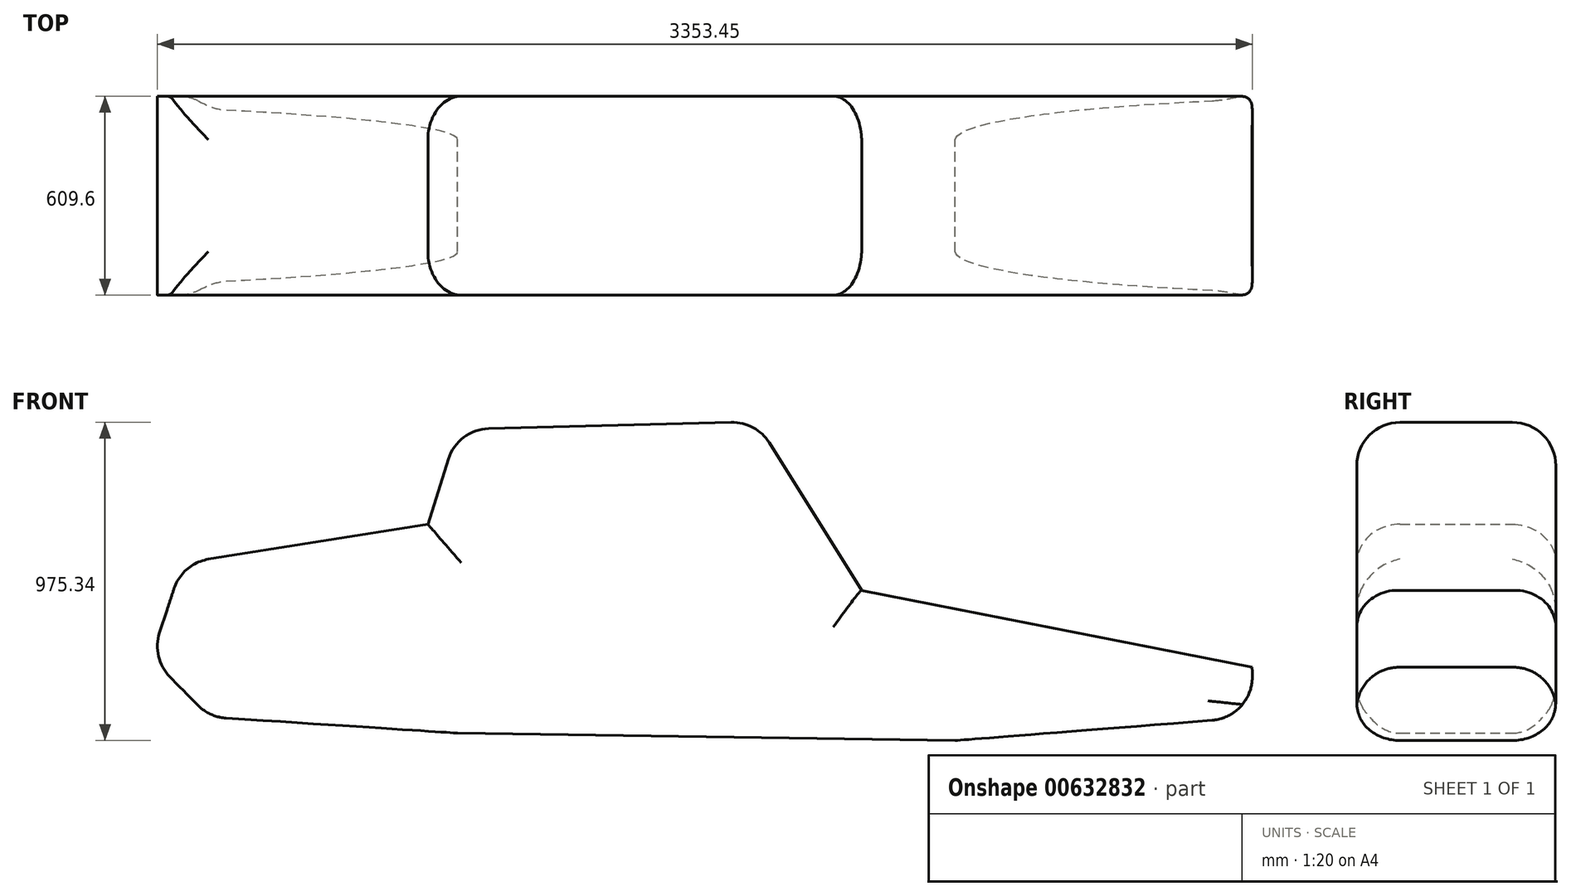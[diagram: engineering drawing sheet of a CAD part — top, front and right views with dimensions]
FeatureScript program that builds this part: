
annotation { "Feature Type Name" : "Feature", "Feature Type Description" : "" }
export const myFeature = defineFeature(function(context is Context, id is Id, definition is map)
    precondition{}
    {
        {
            var Q0;
            Q0=qCreatedBy(makeId("Front.planeOp"),FACE);
            var sketch = newSketch(context, id + "F0", { "sketchPlane" : qUnion([Q0])});
            skLineSegment(sketch, "E0", {"start": v(-2526.52, 590.94) * mm, "end": v(-3279.03, 471.06) * mm});
            skLineSegment(sketch, "E1", {"start": v(-3279.03, 471.06) * mm, "end": v(-3373.67, 181.32) * mm});
            skLineSegment(sketch, "E2", {"start": v(-2526.52, 590.94) * mm, "end": v(-2435.4, 881.8) * mm});
            skLineSegment(sketch, "E3", {"start": v(0, 0) * mm, "end": v(-2.12, 152.39) * mm});
            skLineSegment(sketch, "E4", {"start": v(-2.12, 152.39) * mm, "end": v(-1198.27, 388.33) * mm});
            skLineSegment(sketch, "E5", {"start": v(-1198.27, 388.33) * mm, "end": v(-1521.3, 905.3) * mm});
            skLineSegment(sketch, "E6", {"start": v(-1521.3, 905.3) * mm, "end": v(-2435.4, 881.8) * mm});
            skPoint(sketch, "E7.end.orphan", {"position": v(-2435.4, -49.28) * mm});
            skLineSegment(sketch, "E8", {"start": v(0, 0) * mm, "end": v(-911.57, -71.94) * mm});
            skPoint(sketch, "E9.start.orphan", {"position": v(-3279.03, 0) * mm});
            skLineSegment(sketch, "E10", {"start": v(-3373.67, 181.32) * mm, "end": v(-3195.8, 0) * mm});
            skLineSegment(sketch, "E11", {"start": v(-3195.8, 0) * mm, "end": v(-2435.4, -49.28) * mm});
            skLineSegment(sketch, "E12", {"start": v(-911.57, -71.94) * mm, "end": v(-2435.4, -49.28) * mm});
            skSolve(sketch);
        }
        {
            var Q0;
            Q0=makeQuery(id+"F0.imprint","IMPRINT",FACE,{"disambiguationData":[TD([[makeQuery(id+"F0.imprint","IMPRINT",EDGE,{"derivedFrom":sQuery(id+"F0.wireOp",EDGE,"E0")}),1.0]])]});
            extrude(context, id + "F1", {"entities" : qUnion([Q0]), "depth" : 609.6 * mm, "offsetDistance" : 25.4 * mm});
        }
        {
            var Q0;
            Q0=makeQuery(id+"F1.opExtrude","CAP_EDGE",EDGE,{"disambiguationData":[OSD([sQuery(id+"F0.wireOp",EDGE,"E4")])],"isStart":true});
            var Q1;
            Q1=makeQuery(id+"F1.opExtrude","CAP_EDGE",EDGE,{"disambiguationData":[OSD([sQuery(id+"F0.wireOp",EDGE,"E4")])],"isStart":false});
            fillet(context, id + "F2", {"entities" : qUnion([Q0, Q1]), "radius" : 127 * mm, "tangentPropagation" : true, "allowEdgeOverflow" : false});
        }
        {
            var Q0;
            Q0=makeQuery(id+"F1.opExtrude","CAP_EDGE",EDGE,{"disambiguationData":[OSD([sQuery(id+"F0.wireOp",EDGE,"E5")])],"isStart":false});
            var Q1;
            Q1=makeQuery(id+"F1.opExtrude","CAP_EDGE",EDGE,{"disambiguationData":[OSD([sQuery(id+"F0.wireOp",EDGE,"E5")])],"isStart":true});
            var Q2;
            Q2=makeQuery(id+"F1.opExtrude","CAP_EDGE",EDGE,{"disambiguationData":[OSD([sQuery(id+"F0.wireOp",EDGE,"E6")])],"isStart":false});
            var Q3;
            Q3=makeQuery(id+"F1.opExtrude","CAP_EDGE",EDGE,{"disambiguationData":[OSD([sQuery(id+"F0.wireOp",EDGE,"E6")])],"isStart":true});
            var Q4;
            Q4=makeQuery(id+"F1.opExtrude","SWEPT_EDGE",EDGE,{"disambiguationData":[OSD([sQuery(id+"F0.wireOp",EDGE,"E5"),sQuery(id+"F0.wireOp",EDGE,"E6")])]});
            var Q5;
            Q5=makeQuery(id+"F1.opExtrude","SWEPT_EDGE",EDGE,{"disambiguationData":[OSD([sQuery(id+"F0.wireOp",EDGE,"E2"),sQuery(id+"F0.wireOp",EDGE,"E6")])]});
            var Q6;
            Q6=makeQuery(id+"F1.opExtrude","CAP_EDGE",EDGE,{"disambiguationData":[OSD([sQuery(id+"F0.wireOp",EDGE,"E0")])],"isStart":false});
            var Q7;
            Q7=makeQuery(id+"F1.opExtrude","CAP_EDGE",EDGE,{"disambiguationData":[OSD([sQuery(id+"F0.wireOp",EDGE,"E0")])],"isStart":true});
            var Q8;
            Q8=makeQuery(id+"F1.opExtrude","SWEPT_EDGE",EDGE,{"disambiguationData":[OSD([sQuery(id+"F0.wireOp",EDGE,"E0"),sQuery(id+"F0.wireOp",EDGE,"E1")])]});
            var Q9;
            Q9=makeQuery(id+"F1.opExtrude","SWEPT_EDGE",EDGE,{"disambiguationData":[OSD([sQuery(id+"F0.wireOp",EDGE,"E1"),sQuery(id+"F0.wireOp",EDGE,"E10")])]});
            var Q10;
            Q10=makeQuery(id+"F1.opExtrude","SWEPT_EDGE",EDGE,{"disambiguationData":[OSD([sQuery(id+"F0.wireOp",EDGE,"E10"),sQuery(id+"F0.wireOp",EDGE,"E11")])]});
            var Q11;
            Q11=makeQuery(id+"F1.opExtrude","CAP_EDGE",EDGE,{"disambiguationData":[OSD([sQuery(id+"F0.wireOp",EDGE,"E12")])],"isStart":false});
            var Q12;
            Q12=makeQuery(id+"F1.opExtrude","CAP_EDGE",EDGE,{"disambiguationData":[OSD([sQuery(id+"F0.wireOp",EDGE,"E12")])],"isStart":true});
            var Q13;
            Q13=makeQuery(id+"F1.opExtrude","SWEPT_EDGE",EDGE,{"disambiguationData":[OSD([sQuery(id+"F0.wireOp",EDGE,"E3"),sQuery(id+"F0.wireOp",EDGE,"E8")])]});
            var Q14;
            Q14=makeQuery(id+"F1.opExtrude","CAP_EDGE",EDGE,{"disambiguationData":[OSD([sQuery(id+"F0.wireOp",EDGE,"E2")])],"isStart":false});
            var Q15;
            Q15=makeQuery(id+"F1.opExtrude","CAP_EDGE",EDGE,{"disambiguationData":[OSD([sQuery(id+"F0.wireOp",EDGE,"E2")])],"isStart":true});
            fillet(context, id + "F3", {"entities" : qUnion([Q0, Q1, Q2, Q3, Q4, Q5, Q6, Q7, Q8, Q9, Q10, Q11, Q12, Q13, Q14, Q15]), "radius" : 132.95 * mm, "tangentPropagation" : true, "allowEdgeOverflow" : false});
        }
    });
